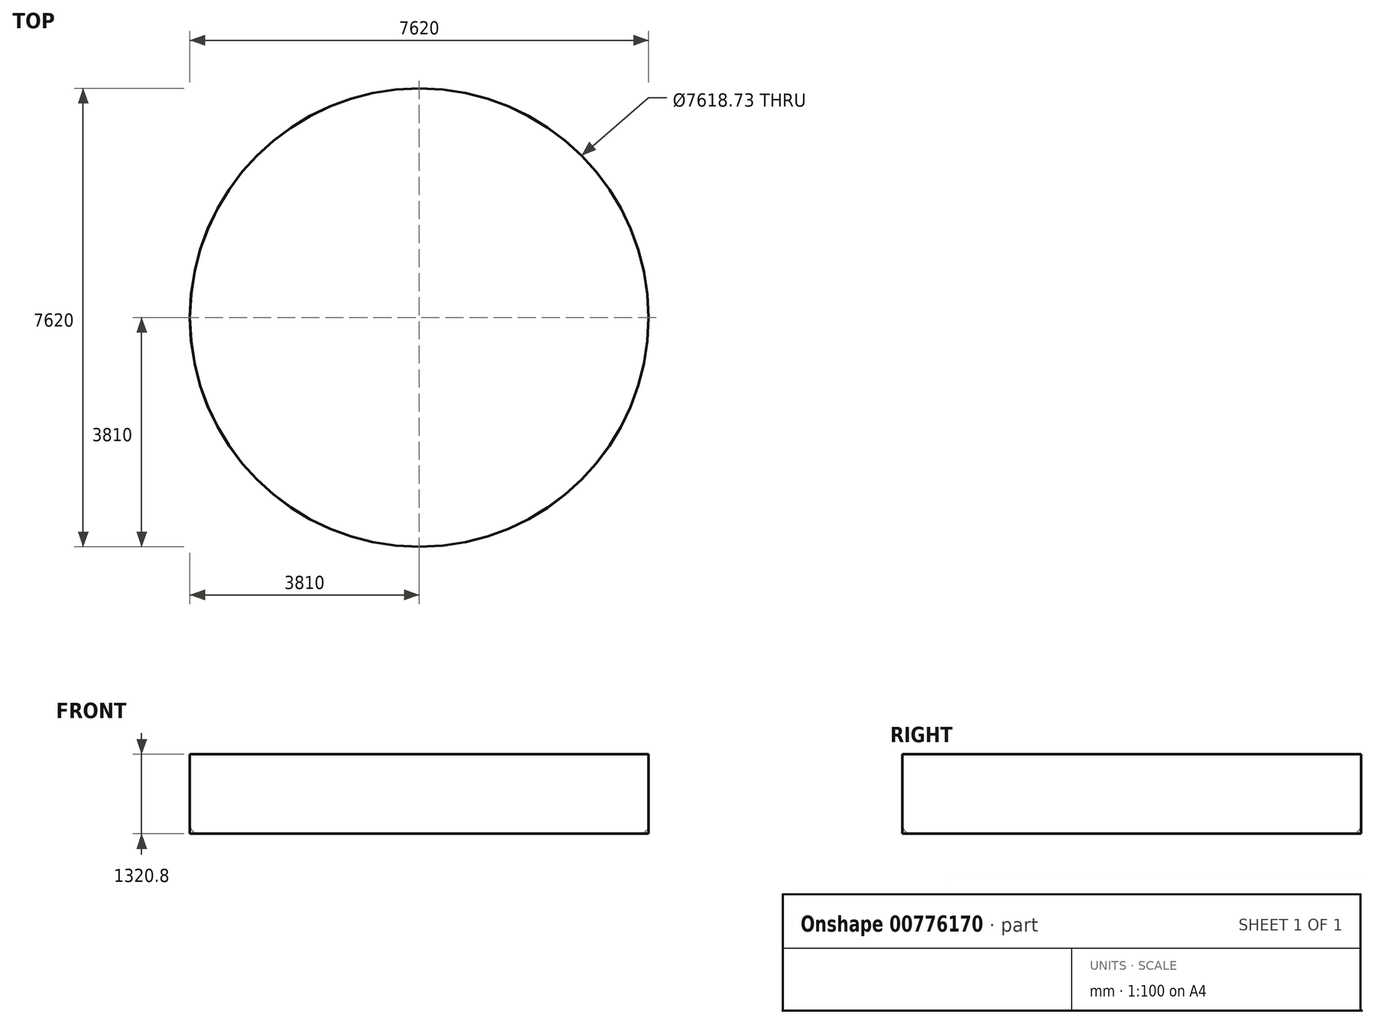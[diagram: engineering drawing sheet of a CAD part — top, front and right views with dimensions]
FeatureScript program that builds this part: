
annotation { "Feature Type Name" : "Feature", "Feature Type Description" : "" }
export const myFeature = defineFeature(function(context is Context, id is Id, definition is map)
    precondition{}
    {
        {
            var Q0;
            Q0=qCreatedBy(makeId("Top.planeOp"),FACE);
            var sketch = newSketch(context, id + "F0", { "sketchPlane" : qUnion([Q0])});
            skCircle(sketch, "E0", {"center": v(0, 0) * mm, "radius": 3810 * mm});
            skSolve(sketch);
        }
        {
            var Q0;
            Q0=makeQuery(id+"F0.imprint","IMPRINT",FACE,{"disambiguationData":[TD([[makeQuery(id+"F0.imprint","IMPRINT",EDGE,{"derivedFrom":sQuery(id+"F0.wireOp",EDGE,"E0")}),1.0]])]});
            extrude(context, id + "F1", {"entities" : qUnion([Q0]), "depth" : 1320.8 * mm, "offsetDistance" : 25.4 * mm});
        }
        {
            var Q0;
            Q0=makeQuery(id+"F1.opExtrude","CAP_FACE",FACE,{"disambiguationData":[OSD([sQuery(id+"F0.wireOp",EDGE,"E0")])],"isStart":false});
            shell(context, id + "F2", {"entities" : qUnion([Q0]), "thickness" : 0.64 * mm});
        }
        {
            var Q0;
            {var subQ0=sQuery(id+"F0.wireOp",EDGE,"E0");Q0=makeQuery(id+"F2.opShell","OFFSET_FACE",FACE,{"disambiguationData":[OSD([subQ0]),TDD([makeQuery(id+"F1.opExtrude","SWEPT_FACE",FACE,{"disambiguationData":[OSD([subQ0])]})])]});}
            var Q1;
            {var subQ0=sQuery(id+"F0.wireOp",EDGE,"E0");Q1=makeQuery(id+"F2.opShell","OFFSET_FACE",FACE,{"disambiguationData":[OSD([subQ0]),TDD([makeQuery(id+"F1.opExtrude","CAP_FACE",FACE,{"disambiguationData":[OSD([subQ0])],"isStart":true})])]});}
            fillet(context, id + "F3", {"entities" : qUnion([Q0, Q1]), "tangentPropagation" : true, "radius" : 152.4 * mm, "defaultsChanged" : false, "vertexSettings" : [], "allowEdgeOverflow" : false});
        }
    });
